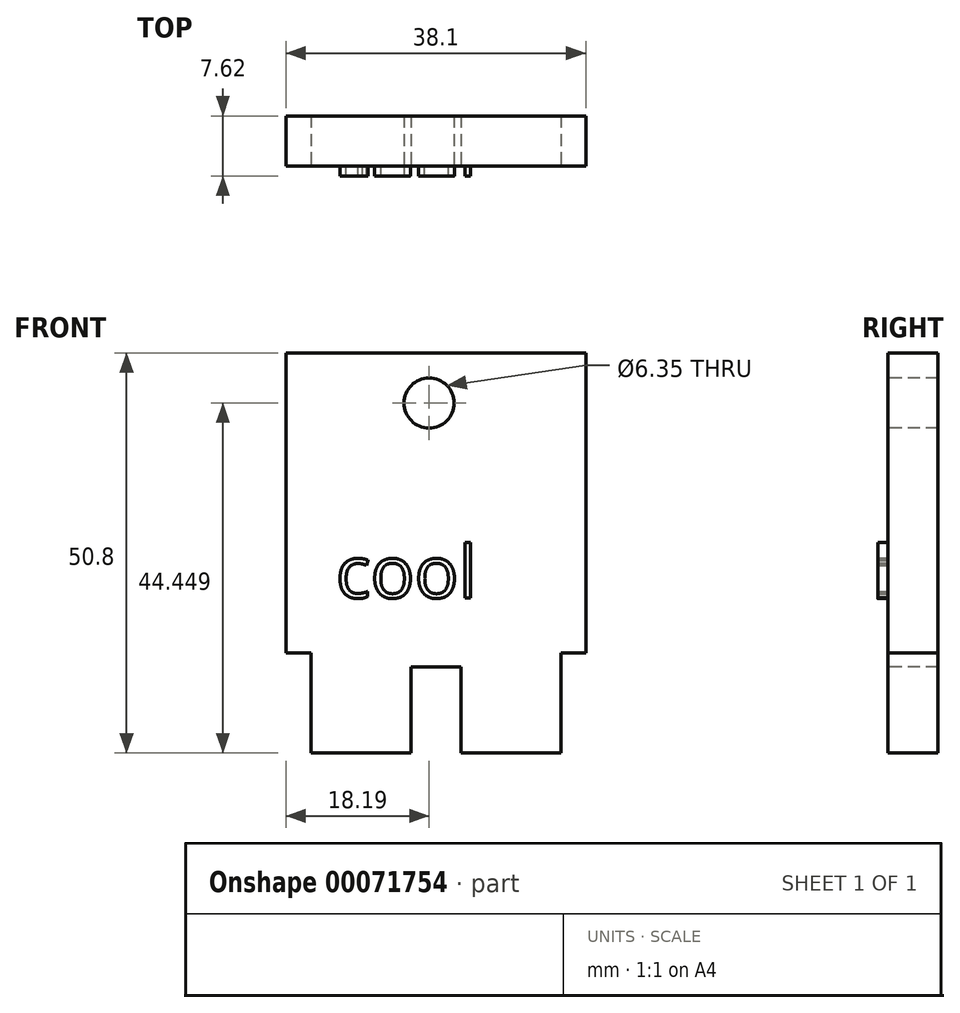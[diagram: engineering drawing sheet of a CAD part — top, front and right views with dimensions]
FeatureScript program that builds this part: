
annotation { "Feature Type Name" : "Feature", "Feature Type Description" : "" }
export const myFeature = defineFeature(function(context is Context, id is Id, definition is map)
    precondition{}
    {
        {
            var Q0;
            Q0=qCreatedBy(makeId("Front.planeOp"),FACE);
            var sketch = newSketch(context, id + "F0", { "sketchPlane" : qUnion([Q0])});
            skLineSegment(sketch, "E0.bottom", {"start": v(-18.2, 41.5) * mm, "end": v(19.9, 41.5) * mm});
            skLineSegment(sketch, "E0.top", {"start": v(-18.2, -9.3) * mm, "end": v(19.9, -9.3) * mm});
            skLineSegment(sketch, "E0.left", {"start": v(-18.2, 41.5) * mm, "end": v(-18.2, -9.3) * mm});
            skLineSegment(sketch, "E0.right", {"start": v(19.9, 41.5) * mm, "end": v(19.9, -9.3) * mm});
            skSolve(sketch);
        }
        {
            var Q0;
            Q0 = qSketchRegion(id + "F0", true);
            extrude(context, id + "F1", {"entities" : qUnion([Q0]), "depth" : 6.35 * mm});
        }
        {
            var Q0;
            Q0=makeQuery(id+"F1.opExtrude","CAP_FACE",FACE,{"disambiguationData":[OSD([sQuery(id+"F0.wireOp",EDGE,"E0.bottom"),sQuery(id+"F0.wireOp",EDGE,"E0.top"),sQuery(id+"F0.wireOp",EDGE,"E0.left"),sQuery(id+"F0.wireOp",EDGE,"E0.right")])],"isStart":false});
            var sketch = newSketch(context, id + "F2", { "sketchPlane" : qUnion([Q0])});
            skLineSegment(sketch, "E1", {"start": v(0, 41.5) * mm, "end": v(0, -9.3) * mm, "construction": true});
            skLineSegment(sketch, "E2", {"start": v(-18.2, 35.15) * mm, "end": v(19.9, 35.15) * mm, "construction": true});
            skCircle(sketch, "E3", {"center": v(0, 35.15) * mm, "radius": 3.18 * mm});
            skSolve(sketch);
        }
        {
            var Q0;
            Q0=makeQuery(id+"F2.imprint","IMPRINT",FACE,{"disambiguationData":[TD([[makeQuery(id+"F2.imprint","IMPRINT",EDGE,{"derivedFrom":sQuery(id+"F2.wireOp",EDGE,"E3")}),1.0]])]});
            extrude(context, id + "F3", {"entities" : qUnion([Q0]), "operationType" : NewBodyOperationType.REMOVE, "endBound" : BoundingType.THROUGH_ALL, "oppositeDirection" : true, "depth" : 6.35 * mm});
        }
        {
            var Q0;
            Q0=makeQuery(id+"F1.opExtrude","CAP_FACE",FACE,{"disambiguationData":[OSD([sQuery(id+"F0.wireOp",EDGE,"E0.bottom"),sQuery(id+"F0.wireOp",EDGE,"E0.top"),sQuery(id+"F0.wireOp",EDGE,"E0.left"),sQuery(id+"F0.wireOp",EDGE,"E0.right")])],"isStart":false});
            var sketch = newSketch(context, id + "F4", { "sketchPlane" : qUnion([Q0])});
            skLineSegment(sketch, "E4.bottom", {"start": v(-18.2, 3.4) * mm, "end": v(-15.02, 3.4) * mm});
            skLineSegment(sketch, "E4.top", {"start": v(-18.2, -9.3) * mm, "end": v(-15.02, -9.3) * mm});
            skLineSegment(sketch, "E4.left", {"start": v(-18.2, 3.4) * mm, "end": v(-18.2, -9.3) * mm});
            skLineSegment(sketch, "E4.right", {"start": v(-15.02, 3.4) * mm, "end": v(-15.02, -9.3) * mm});
            skLineSegment(sketch, "E5.bottom", {"start": v(16.73, 3.4) * mm, "end": v(19.9, 3.4) * mm});
            skLineSegment(sketch, "E5.top", {"start": v(16.73, -9.3) * mm, "end": v(19.9, -9.3) * mm});
            skLineSegment(sketch, "E5.left", {"start": v(16.73, 3.4) * mm, "end": v(16.73, -9.3) * mm});
            skLineSegment(sketch, "E5.right", {"start": v(19.9, 3.4) * mm, "end": v(19.9, -9.3) * mm});
            skSolve(sketch);
        }
        {
            var Q0;
            Q0 = qSketchRegion(id + "F4", true);
            extrude(context, id + "F5", {"entities" : qUnion([Q0]), "operationType" : NewBodyOperationType.REMOVE, "endBound" : BoundingType.THROUGH_ALL, "oppositeDirection" : true, "depth" : 25.4 * mm});
        }
        {
            var Q0;
            Q0=makeQuery(id+"F1.opExtrude","CAP_FACE",FACE,{"disambiguationData":[OSD([sQuery(id+"F0.wireOp",EDGE,"E0.bottom"),sQuery(id+"F0.wireOp",EDGE,"E0.top"),sQuery(id+"F0.wireOp",EDGE,"E0.left"),sQuery(id+"F0.wireOp",EDGE,"E0.right")])],"isStart":false});
            var sketch = newSketch(context, id + "F6", { "sketchPlane" : qUnion([Q0])});
            skSolve(sketch);
        }
        {
            var Q0;
            Q0=makeQuery(id+"F6.imprint","IMPRINT",FACE,{"disambiguationData":[TD([[makeQuery(id+"F6.imprint","IMPRINT",EDGE,{"derivedFrom":makeQuery(id+"F1.opExtrude","CAP_EDGE",EDGE,{"disambiguationData":[OSD([sQuery(id+"F0.wireOp",EDGE,"E0.bottom")])],"isStart":false})}),-1.0]])]});
            var sketch = newSketch(context, id + "F7", { "sketchPlane" : qUnion([Q0])});
            skLineSegment(sketch, "E6.bottom", {"start": v(-2.32, 1.63) * mm, "end": v(4.03, 1.63) * mm});
            skLineSegment(sketch, "E6.top", {"start": v(-2.32, -11.07) * mm, "end": v(4.03, -11.07) * mm});
            skLineSegment(sketch, "E6.left", {"start": v(-2.32, 1.63) * mm, "end": v(-2.32, -11.07) * mm});
            skLineSegment(sketch, "E6.right", {"start": v(4.03, 1.63) * mm, "end": v(4.03, -11.07) * mm});
            skSolve(sketch);
        }
        {
            var Q0;
            Q0 = qSketchRegion(id + "F7", true);
            extrude(context, id + "F8", {"entities" : qUnion([Q0]), "operationType" : NewBodyOperationType.REMOVE, "endBound" : BoundingType.THROUGH_ALL, "oppositeDirection" : true, "depth" : 25.4 * mm});
        }
        {
            var Q0;
            Q0=makeQuery(id+"F6.imprint","IMPRINT",FACE,{"disambiguationData":[TD([[makeQuery(id+"F6.imprint","IMPRINT",EDGE,{"derivedFrom":makeQuery(id+"F1.opExtrude","CAP_EDGE",EDGE,{"disambiguationData":[OSD([sQuery(id+"F0.wireOp",EDGE,"E0.bottom")])],"isStart":false})}),-1.0]])]});
            var sketch = newSketch(context, id + "F9", { "sketchPlane" : qUnion([Q0])});
            skText(sketch, "E7", { "text": "cool", "fontName": "OpenSans-Regular.ttf"});
            const initialGuessF9  = {"E7": [-0.01184, 0.01039, 1, 0, 0.00666]};
            skSetInitialGuess(sketch, initialGuessF9);
            skSolve(sketch);
        }
        {
            var Q0;
            Q0=makeQuery(id+"F9.imprint","IMPRINT",FACE,{"disambiguationData":[TD([[makeQuery(id+"F9.imprint","IMPRINT",EDGE,{"derivedFrom":sQuery(id+"F9.wireOp",EDGE,"E7.sketch_text.stroke-0")}),-1.0]])]});
            var Q1;
            Q1=makeQuery(id+"F9.imprint","IMPRINT",FACE,{"disambiguationData":[TD([[makeQuery(id+"F9.imprint","IMPRINT",EDGE,{"derivedFrom":sQuery(id+"F9.wireOp",EDGE,"E7.sketch_text.stroke-49")}),-1.0]])]});
            var Q2;
            Q2=makeQuery(id+"F9.imprint","IMPRINT",FACE,{"disambiguationData":[TD([[makeQuery(id+"F9.imprint","IMPRINT",EDGE,{"derivedFrom":sQuery(id+"F9.wireOp",EDGE,"E7.sketch_text.stroke-15")}),-1.0]])]});
            var Q3;
            Q3=makeQuery(id+"F9.imprint","IMPRINT",FACE,{"disambiguationData":[TD([[makeQuery(id+"F9.imprint","IMPRINT",EDGE,{"derivedFrom":sQuery(id+"F9.wireOp",EDGE,"E7.sketch_text.stroke-32")}),-1.0]])]});
            extrude(context, id + "F10", {"entities" : qUnion([Q0, Q1, Q2, Q3]), "operationType" : NewBodyOperationType.ADD, "depth" : 1.27 * mm});
        }
    });
